# Revit family: 601-A-005-DN350-400
name_source: partatom
category: Pipe Accessories
units: mm (PartAtom-declared; Revit-internal decimal feet)

## family parameters
Always vertical = Yes
Cut with Voids When Loaded = No
Part Type = Valve - Breaks Into
Round Connector Dimension = Use Diameter
Shared = No
Work Plane-Based = No

## types (5) — shared parameters
B2 = 116 mm  [stored 0.380577 ft]
Body_height = 231 mm  [stored 0.757874 ft]
Body_height_ref = 219 mm
DN350_352-378 = 601-378-000-4100
DN350_372-396 = 601-396-000-4100
DN350_384-410 = 601-410-000-4100
DN400_410-436 = 601-436-000-4100
DN400_436-462 = 601-462-000-4100
Description_ = AVK UNIVERSAL SUPA® STRAIGHT COUPLING
F = 5 mm  [stored 0.0164042 ft]
L = 270 mm  [stored 0.885827 ft]
L1 = 160 mm  [stored 0.524934 ft]
Search_Table = 601-A-005-DN350-400
URL_product_pages = https://www.avkvalves.com
W1 = 32 mm  [stored 0.104987 ft]

## per-type parameters (varying)
| type | D1 | D2 | D3 | D3_Ref | DN | DN2 | DN_Ref | ID | PCD | PCD_Ref | PCD_Ref_2 | W2 |
| DN350_372-396 | 237 mm  [stored 0.777559 ft] | 215 mm | 530 mm | 518 mm | 350 mm  [stored 1.14829 ft] | 397 mm | 199 mm | 175 mm  [stored 0.574147 ft] | 494 mm | 474 mm | 518 mm | 260 mm  [stored 0.853018 ft] |
| DN350_384-410 | 237 mm  [stored 0.777559 ft] | 215 mm | 530 mm | 518 mm | 350 mm  [stored 1.14829 ft] | 410 mm  [stored 1.34514 ft] | 205 mm | 175 mm  [stored 0.574147 ft] | 494 mm | 474 mm | 518 mm | 260 mm  [stored 0.853018 ft] |
| DN400_410-436 | 250 mm  [stored 0.82021 ft] | 227 mm  [stored 0.744751 ft] | 556 mm | 544 mm | 400 mm  [stored 1.31234 ft] | 436 mm | 218 mm | 200 mm  [stored 0.656168 ft] | 520 mm | 500 mm  [stored 1.64042 ft] | 544 mm | 273 mm  [stored 0.895669 ft] |
| DN400_436-462 | 263 mm  [stored 0.862861 ft] | 239 mm | 582 mm | 570 mm | 400 mm  [stored 1.31234 ft] | 462 mm  [stored 1.51575 ft] | 231 mm  [stored 0.757874 ft] | 200 mm  [stored 0.656168 ft] | 546 mm | 526 mm | 570 mm | 286 mm  [stored 0.93832 ft] |
| DN350_352-378 | 228 mm  [stored 0.748031 ft] | 207 mm | 513 mm | 501 mm  [stored 1.6437 ft] | 350 mm  [stored 1.14829 ft] | 378 mm | 189 mm | 175 mm  [stored 0.574147 ft] | 476 mm | 456 mm  [stored 1.49606 ft] | 500 mm  [stored 1.64042 ft] | 252 mm |

note: [stored X ft] marks values corroborated as IEEE doubles in the binary element streams (Revit-internal decimal feet)

## geometry (parser evidence)
native form markers: Sweep x11
no freeform markers — native parametric forms only
